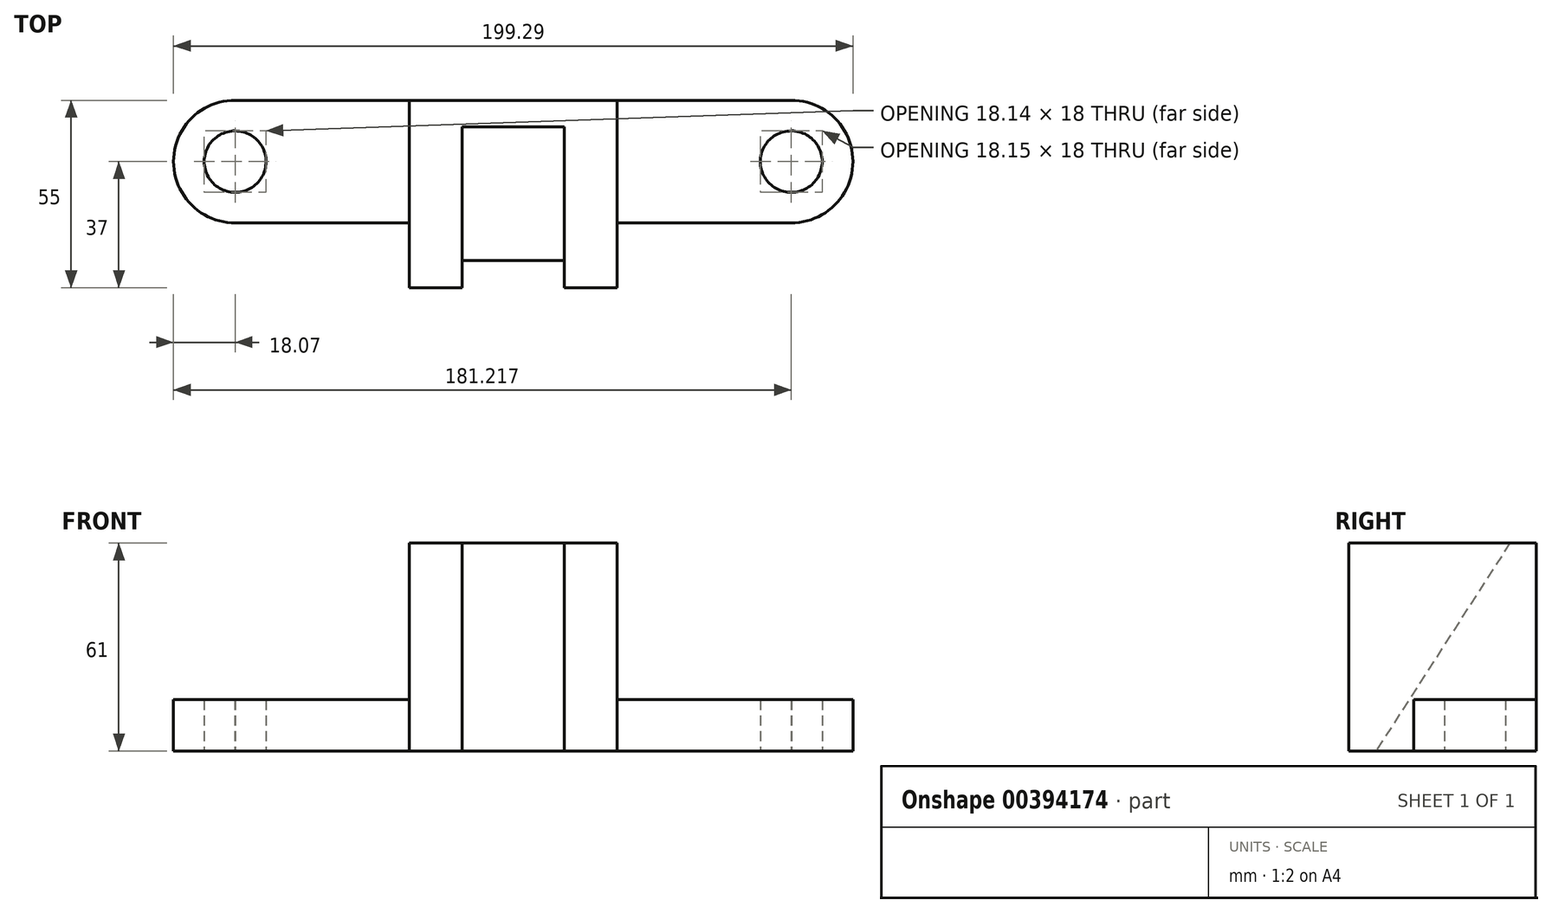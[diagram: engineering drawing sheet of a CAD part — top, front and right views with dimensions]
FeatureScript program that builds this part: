
annotation { "Feature Type Name" : "Feature", "Feature Type Description" : "" }
export const myFeature = defineFeature(function(context is Context, id is Id, definition is map)
    precondition{}
    {
        {
            var Q0;
            Q0=qCreatedBy(makeId("Front.planeOp"),FACE);
            var sketch = newSketch(context, id + "F0", { "sketchPlane" : qUnion([Q0])});
            skLineSegment(sketch, "E0.bottom", {"start": v(-30.5, 61) * mm, "end": v(30.5, 61) * mm});
            skLineSegment(sketch, "E0.top", {"start": v(-81.5, 0) * mm, "end": v(81.5, 0) * mm});
            skLineSegment(sketch, "E0.left", {"start": v(-81.5, 15) * mm, "end": v(-81.5, 0) * mm});
            skLineSegment(sketch, "E0.right", {"start": v(81.5, 15) * mm, "end": v(81.5, 0) * mm});
            skLineSegment(sketch, "E1.top", {"start": v(-81.5, 15) * mm, "end": v(-30.5, 15) * mm});
            skLineSegment(sketch, "E1.right", {"start": v(-30.5, 61) * mm, "end": v(-30.5, 15) * mm});
            skLineSegment(sketch, "E2.top", {"start": v(81.5, 15) * mm, "end": v(30.5, 15) * mm});
            skLineSegment(sketch, "E2.right", {"start": v(30.5, 61) * mm, "end": v(30.5, 15) * mm});
            skSolve(sketch);
        }
        {
            var Q0;
            Q0=qSketchRegion(id+"F0",true);
            extrude(context, id + "F1", {"entities" : qUnion([Q0]), "depth" : 55 * mm});
        }
        {
            var Q0;
            Q0=qCreatedBy(makeId("Top.planeOp"),FACE);
            var sketch = newSketch(context, id + "F2", { "sketchPlane" : qUnion([Q0])});
            skCircle(sketch, "E3", {"center": v(-81.64, -18) * mm, "radius": 18 * mm});
            skCircle(sketch, "E4", {"center": v(81.65, -18) * mm, "radius": 18 * mm});
            skPoint(sketch, "E5.orphan", {"position": v(-15, -7.75) * mm});
            skPoint(sketch, "E6.orphan", {"position": v(15, -7.75) * mm});
            skPoint(sketch, "E7.end.orphan", {"position": v(15, -47) * mm});
            skPoint(sketch, "E7.start.orphan", {"position": v(-15, -47) * mm});
            skPoint(sketch, "E8.end.orphan", {"position": v(81.5, -36) * mm});
            skPoint(sketch, "E8.start.orphan", {"position": v(-81.5, -36) * mm});
            skCircle(sketch, "E9", {"center": v(-81.64, -18) * mm, "radius": 9 * mm});
            skCircle(sketch, "E10", {"center": v(81.65, -18) * mm, "radius": 9 * mm});
            skSolve(sketch);
        }
        {
            var Q0;
            Q0=qSketchRegion(id+"F2",true);
            extrude(context, id + "F3", {"entities" : qUnion([Q0]), "operationType" : NewBodyOperationType.ADD, "depth" : 15 * mm});
        }
        {
            var Q0;
            Q0=qCreatedBy(makeId("Top.planeOp"),FACE);
            var sketch = newSketch(context, id + "F4", { "sketchPlane" : qUnion([Q0])});
            skCircle(sketch, "E11", {"center": v(-81.5, -18) * mm, "radius": 9 * mm});
            skCircle(sketch, "E12", {"center": v(81.5, -18) * mm, "radius": 9 * mm});
            skLineSegment(sketch, "E13.bottom", {"start": v(-81.5, -36) * mm, "end": v(-30.5, -36) * mm});
            skLineSegment(sketch, "E13.top", {"start": v(-81.5, -55) * mm, "end": v(-30.5, -55) * mm});
            skLineSegment(sketch, "E13.left", {"start": v(-81.5, -36) * mm, "end": v(-81.5, -55) * mm});
            skLineSegment(sketch, "E13.right", {"start": v(-30.5, -36) * mm, "end": v(-30.5, -55) * mm});
            skLineSegment(sketch, "E14", {"start": v(81.5, -55) * mm, "end": v(30.5, -55) * mm});
            skPoint(sketch, "E15.right.start.orphan", {"position": v(81.5, -47) * mm});
            skPoint(sketch, "E15.left.start.orphan", {"position": v(30.5, -47) * mm});
            skLineSegment(sketch, "E16", {"start": v(81.5, -36) * mm, "end": v(81.5, -55) * mm});
            skLineSegment(sketch, "E17", {"start": v(30.5, -36) * mm, "end": v(30.5, -55) * mm});
            skLineSegment(sketch, "E18", {"start": v(30.5, -36) * mm, "end": v(81.5, -36) * mm});
            skSolve(sketch);
        }
        {
            var Q0;
            Q0=qSketchRegion(id+"F4",true);
            extrude(context, id + "F5", {"entities" : qUnion([Q0]), "operationType" : NewBodyOperationType.REMOVE, "depth" : 15 * mm});
        }
        {
            var Q0;
            Q0=makeQuery(id+"F5.boolean.opBoolean","MERGE",FACE,{"derivedFrom":[makeQuery(id+"F1.opExtrude","SWEPT_FACE",FACE,{"disambiguationData":[OSD([sQuery(id+"F0.wireOp",EDGE,"E1.right")])]}),makeQuery(id+"F5.opExtrude","SWEPT_FACE",FACE,{"disambiguationData":[OSD([sQuery(id+"F4.wireOp",EDGE,"E13.right")])]})]});
            var sketch = newSketch(context, id + "F6", { "sketchPlane" : qUnion([Q0])});
            skLineSegment(sketch, "E19", {"start": v(7.75, 61) * mm, "end": v(47, 0) * mm});
            skLineSegment(sketch, "E20", {"start": v(7.75, 61) * mm, "end": v(55, 61) * mm});
            skLineSegment(sketch, "E21", {"start": v(55, 61) * mm, "end": v(55, 0) * mm});
            skLineSegment(sketch, "E22", {"start": v(55, 0) * mm, "end": v(47, 0) * mm});
            skSolve(sketch);
        }
        {
            var Q0;
            Q0=qSketchRegion(id+"F6",true);
            extrude(context, id + "F7", {"entities" : qUnion([Q0]), "operationType" : NewBodyOperationType.REMOVE, "oppositeDirection" : true, "depth" : 45.5 * mm, "hasSecondDirection" : true, "secondDirectionOppositeDirection" : true, "secondDirectionDepth" : 15.5 * mm});
        }
    });
